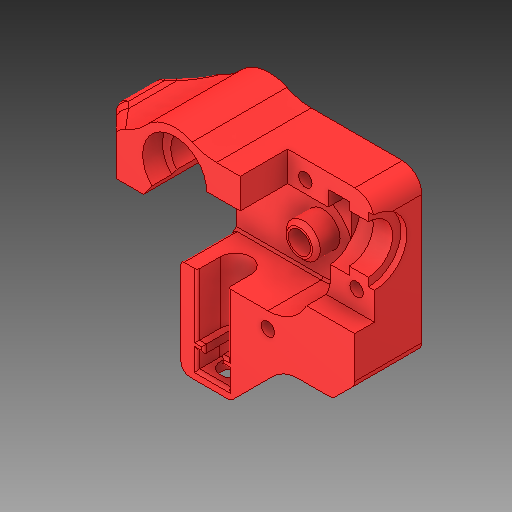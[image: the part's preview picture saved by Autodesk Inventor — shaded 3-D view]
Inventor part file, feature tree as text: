
AUTODESK INVENTOR PART (.ipt)
format: ipt  version: 2019 (Build 230136000, 136)  size: 825,344 bytes
history: native  units: mm
features: thicken_offset x13, fillet x3, move_body x3, direct_edit x1, chamfer x1
ambient origin geometry x8: Origin, YZ Plane, XZ Plane, XY Plane, X Axis, Y Axis, Z Axis, Center Point
bodies: Solid1 (feature_tree)
feature tree (21):
  thicken_offset  "Thicken1"
  thicken_offset  "Thicken2"
  thicken_offset  "Thicken3"
  thicken_offset  "Thicken4"
  thicken_offset  "Thicken5"
  direct_edit  "Direct Edit1"
  thicken_offset  "Thicken6"
  thicken_offset  "Thicken7"
  thicken_offset  "Thicken8"
  thicken_offset  "Thicken9"
  thicken_offset  "Thicken10"
  thicken_offset  "Thicken11"
  thicken_offset  "Thicken12"
  thicken_offset  "Thicken13"
  fillet  "Fillet1"  Radius=1.0mm
  chamfer  "Chamfer1"  Distance=1.0mm
  fillet  "Fillet3"  Radius=1.0mm
  fillet  "Fillet6"  Radius=1.0mm
  move_body  "Move1"
  move_body  "Move2"
  move_body  "Move3"
